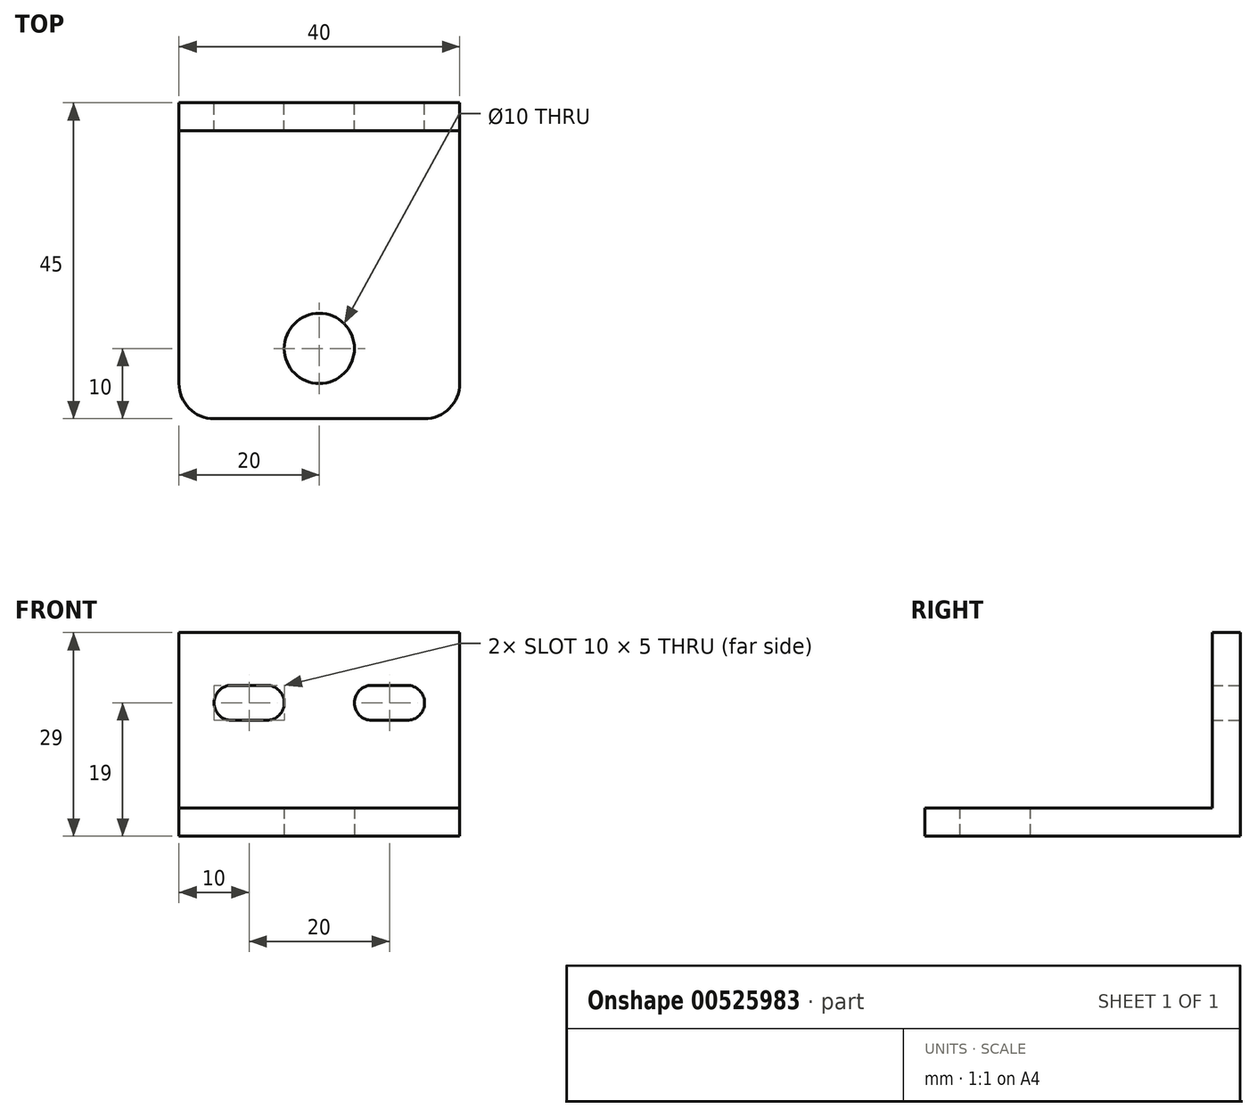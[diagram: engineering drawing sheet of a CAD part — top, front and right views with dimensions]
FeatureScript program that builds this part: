
annotation { "Feature Type Name" : "Feature", "Feature Type Description" : "" }
export const myFeature = defineFeature(function(context is Context, id is Id, definition is map)
    precondition{}
    {
        {
            var Q0;
            Q0=qCreatedBy(makeId("Top.planeOp"),FACE);
            var sketch = newSketch(context, id + "F0", { "sketchPlane" : qUnion([Q0])});
            skLineSegment(sketch, "E0.bottom", {"start": v(-5, 0) * mm, "end": v(-35, 0) * mm});
            skLineSegment(sketch, "E0.top", {"start": v(0, 45) * mm, "end": v(-40, 45) * mm});
            skLineSegment(sketch, "E0.left", {"start": v(0, 5) * mm, "end": v(0, 45) * mm});
            skLineSegment(sketch, "E0.right", {"start": v(-40, 5) * mm, "end": v(-40, 45) * mm});
            skPoint(sketch, "E1.visualSharp", {"position": v(-40, 0) * mm});
            skArc(sketch, "E1.filletArc", {"start": v(-40, 5) * mm, "mid": v(-38.54, 1.46) * mm, "end": v(-35, 0) * mm});
            skPoint(sketch, "E2.visualSharp", {"position": v(0, 0) * mm});
            skArc(sketch, "E2.filletArc", {"start": v(-5, 0) * mm, "mid": v(-1.46, 1.46) * mm, "end": v(0, 5) * mm});
            skSolve(sketch);
        }
        {
            var Q0;
            Q0 = qSketchRegion(id + "F0", true);
            extrude(context, id + "F1", {"entities" : qUnion([Q0]), "depth" : 4 * mm, "offsetDistance" : 25 * mm});
        }
        {
            var Q0;
            Q0=makeQuery(id+"F1.opExtrude","CAP_FACE",FACE,{"disambiguationData":[OSD([sQuery(id+"F0.wireOp",EDGE,"E0.bottom"),sQuery(id+"F0.wireOp",EDGE,"E0.top"),sQuery(id+"F0.wireOp",EDGE,"E0.left"),sQuery(id+"F0.wireOp",EDGE,"E0.right")])],"isStart":false});
            var sketch = newSketch(context, id + "F2", { "sketchPlane" : qUnion([Q0])});
            skLineSegment(sketch, "E3.bottom", {"start": v(-40, 45) * mm, "end": v(0, 45) * mm});
            skLineSegment(sketch, "E3.top", {"start": v(-40, 41) * mm, "end": v(0, 41) * mm});
            skLineSegment(sketch, "E3.left", {"start": v(-40, 45) * mm, "end": v(-40, 41) * mm});
            skLineSegment(sketch, "E3.right", {"start": v(0, 45) * mm, "end": v(0, 41) * mm});
            skSolve(sketch);
        }
        {
            var Q0;
            Q0 = qSketchRegion(id + "F2", true);
            extrude(context, id + "F3", {"entities" : qUnion([Q0]), "operationType" : NewBodyOperationType.ADD, "depth" : 25 * mm, "offsetDistance" : 25 * mm});
        }
        {
            var Q0;
            Q0=makeQuery(id+"F3.boolean.opBoolean","MERGE",FACE,{"derivedFrom":[makeQuery(id+"F1.opExtrude","SWEPT_FACE",FACE,{"disambiguationData":[OSD([sQuery(id+"F0.wireOp",EDGE,"E0.top")])]}),makeQuery(id+"F3.opExtrude","SWEPT_FACE",FACE,{"disambiguationData":[OSD([sQuery(id+"F2.wireOp",EDGE,"E3.bottom")])]})]});
            var sketch = newSketch(context, id + "F4", { "sketchPlane" : qUnion([Q0])});
            skLineSegment(sketch, "E4", {"start": v(40, 19) * mm, "end": v(0, 19) * mm, "construction": true});
            skLineSegment(sketch, "E5.bottom", {"start": v(27.5, 16.5) * mm, "end": v(32.5, 16.5) * mm});
            skLineSegment(sketch, "E5.top", {"start": v(27.5, 21.5) * mm, "end": v(32.5, 21.5) * mm});
            skLineSegment(sketch, "E5.left", {"start": v(25, 19) * mm, "end": v(25, 19) * mm});
            skLineSegment(sketch, "E5.right", {"start": v(35, 19) * mm, "end": v(35, 19) * mm});
            skPoint(sketch, "E5.middle", {"position": v(30, 19) * mm});
            skLineSegment(sketch, "E6.bottom", {"start": v(7.5, 16.5) * mm, "end": v(12.5, 16.5) * mm});
            skLineSegment(sketch, "E6.top", {"start": v(7.5, 21.5) * mm, "end": v(12.5, 21.5) * mm});
            skLineSegment(sketch, "E6.left", {"start": v(5, 19) * mm, "end": v(5, 19) * mm});
            skLineSegment(sketch, "E6.right", {"start": v(15, 19) * mm, "end": v(15, 19) * mm});
            skPoint(sketch, "E6.middle", {"position": v(10, 19) * mm});
            skPoint(sketch, "E7.visualSharp", {"position": v(35, 16.5) * mm});
            skArc(sketch, "E7.filletArc", {"start": v(32.5, 16.5) * mm, "mid": v(34.27, 17.23) * mm, "end": v(35, 19) * mm});
            skPoint(sketch, "E8.visualSharp", {"position": v(35, 21.5) * mm});
            skArc(sketch, "E8.filletArc", {"start": v(35, 19) * mm, "mid": v(34.27, 20.77) * mm, "end": v(32.5, 21.5) * mm});
            skPoint(sketch, "E9.visualSharp", {"position": v(25, 16.5) * mm});
            skArc(sketch, "E9.filletArc", {"start": v(25, 19) * mm, "mid": v(25.73, 17.23) * mm, "end": v(27.5, 16.5) * mm});
            skPoint(sketch, "E10.visualSharp", {"position": v(25, 21.5) * mm});
            skArc(sketch, "E10.filletArc", {"start": v(27.5, 21.5) * mm, "mid": v(25.73, 20.77) * mm, "end": v(25, 19) * mm});
            skPoint(sketch, "E11.visualSharp", {"position": v(15, 16.5) * mm});
            skArc(sketch, "E11.filletArc", {"start": v(12.5, 16.5) * mm, "mid": v(14.27, 17.23) * mm, "end": v(15, 19) * mm});
            skPoint(sketch, "E12.visualSharp", {"position": v(15, 21.5) * mm});
            skArc(sketch, "E12.filletArc", {"start": v(15, 19) * mm, "mid": v(14.27, 20.77) * mm, "end": v(12.5, 21.5) * mm});
            skPoint(sketch, "E13.visualSharp", {"position": v(5, 21.5) * mm});
            skArc(sketch, "E13.filletArc", {"start": v(7.5, 21.5) * mm, "mid": v(5.73, 20.77) * mm, "end": v(5, 19) * mm});
            skPoint(sketch, "E14.visualSharp", {"position": v(5, 16.5) * mm});
            skArc(sketch, "E14.filletArc", {"start": v(5, 19) * mm, "mid": v(5.73, 17.23) * mm, "end": v(7.5, 16.5) * mm});
            skSolve(sketch);
        }
        {
            var Q0;
            Q0 = qSketchRegion(id + "F4", true);
            extrude(context, id + "F5", {"entities" : qUnion([Q0]), "operationType" : NewBodyOperationType.REMOVE, "oppositeDirection" : true, "depth" : 25 * mm, "offsetDistance" : 25 * mm});
        }
        {
            var Q0;
            Q0=makeQuery(id+"F1.opExtrude","CAP_FACE",FACE,{"disambiguationData":[OSD([sQuery(id+"F0.wireOp",EDGE,"E0.bottom"),sQuery(id+"F0.wireOp",EDGE,"E0.top"),sQuery(id+"F0.wireOp",EDGE,"E0.left"),sQuery(id+"F0.wireOp",EDGE,"E0.right"),sQuery(id+"F0.wireOp",EDGE,"E1.filletArc"),sQuery(id+"F0.wireOp",EDGE,"E2.filletArc")])],"isStart":true});
            var sketch = newSketch(context, id + "F6", { "sketchPlane" : qUnion([Q0])});
            skLineSegment(sketch, "E15", {"start": v(-20, -45) * mm, "end": v(-20, 0) * mm, "construction": true});
            skCircle(sketch, "E16", {"center": v(-20, -10) * mm, "radius": 5 * mm});
            skSolve(sketch);
        }
        {
            var Q0;
            Q0 = qSketchRegion(id + "F6", true);
            extrude(context, id + "F7", {"entities" : qUnion([Q0]), "operationType" : NewBodyOperationType.REMOVE, "oppositeDirection" : true, "depth" : 25 * mm, "offsetDistance" : 25 * mm});
        }
    });
